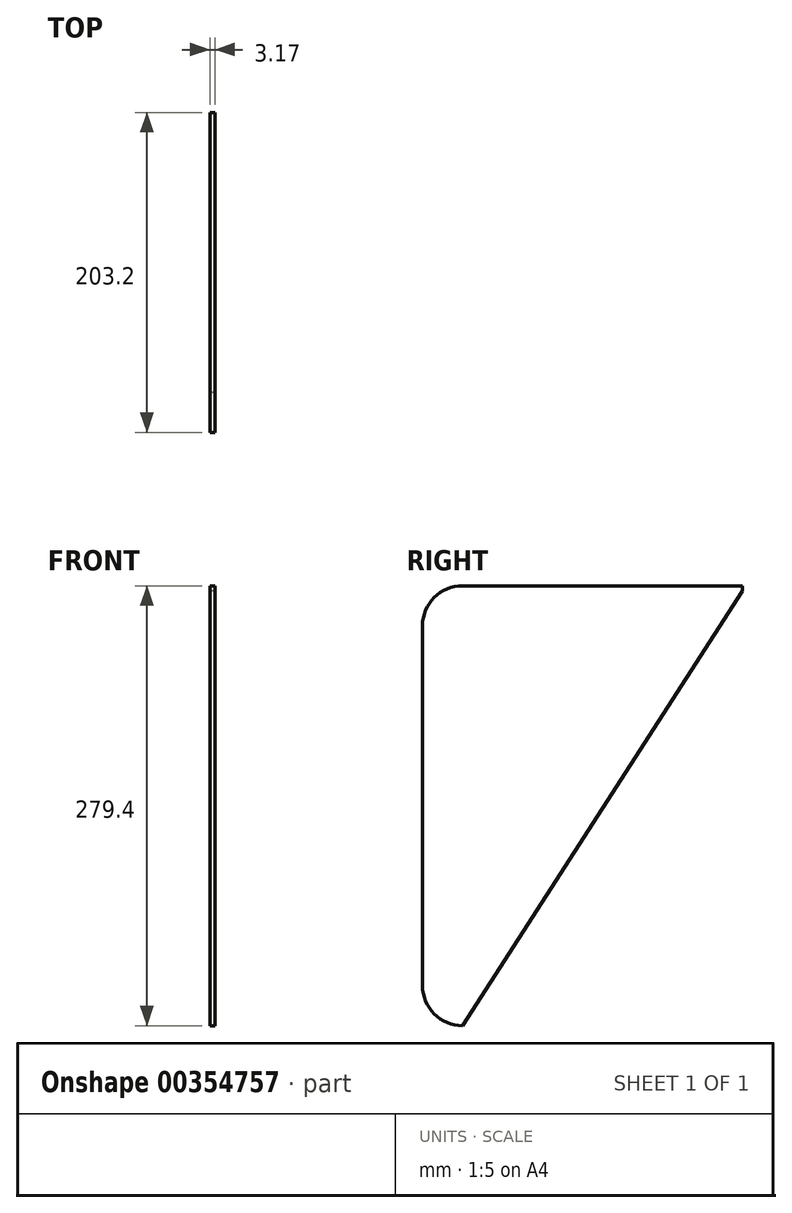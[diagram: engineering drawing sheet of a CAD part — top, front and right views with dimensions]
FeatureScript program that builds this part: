
annotation { "Feature Type Name" : "Feature", "Feature Type Description" : "" }
export const myFeature = defineFeature(function(context is Context, id is Id, definition is map)
    precondition{}
    {
        {
            var Q0;
            Q0=qCreatedBy(makeId("Right.planeOp"),FACE);
            var sketch = newSketch(context, id + "F0", { "sketchPlane" : qUnion([Q0])});
            skLineSegment(sketch, "E0.bottom", {"start": v(88.9, 1.59) * mm, "end": v(-88.9, 1.59) * mm});
            skLineSegment(sketch, "E0.top", {"start": v(88.9, -1.59) * mm, "end": v(-88.9, -1.59) * mm});
            skLineSegment(sketch, "E0.left", {"start": v(88.9, 1.59) * mm, "end": v(88.9, -1.59) * mm});
            skLineSegment(sketch, "E0.right", {"start": v(-88.9, 1.59) * mm, "end": v(-88.9, -1.59) * mm});
            skPoint(sketch, "E0.middle", {"position": v(0, 0) * mm});
            skArc(sketch, "E1", {"start": v(-88.9, 1.59) * mm, "mid": v(-106.86, -5.85) * mm, "end": v(-114.3, -23.81) * mm});
            skArc(sketch, "E2.0", {"start": v(-87.88, -1.61) * mm, "mid": v(-104.25, -7.74) * mm, "end": v(-111.13, -23.81) * mm});
            skLineSegment(sketch, "E3", {"start": v(-114.3, -23.81) * mm, "end": v(-111.13, -23.81) * mm});
            skLineSegment(sketch, "E4", {"start": v(-114.3, -23.81) * mm, "end": v(-114.3, -252.41) * mm});
            skLineSegment(sketch, "E5", {"start": v(-111.13, -23.81) * mm, "end": v(-111.13, -248.5) * mm});
            skLineSegment(sketch, "E6", {"start": v(-114.3, -252.41) * mm, "end": v(-111.13, -248.5) * mm});
            skPoint(sketch, "E7.start.orphan", {"position": v(-111.13, -252.41) * mm});
            skArc(sketch, "E8", {"start": v(-114.3, -252.41) * mm, "mid": v(-106.89, -270.34) * mm, "end": v(-88.98, -277.81) * mm});
            skLineSegment(sketch, "E9", {"start": v(-88.98, -277.81) * mm, "end": v(88.9, -1.59) * mm});
            skSolve(sketch);
        }
        {
            var Q0;
            Q0 = qSketchRegion(id + "F0", true);
            extrude(context, id + "F1", {"entities" : qUnion([Q0]), "depth" : 3.17 * mm});
        }
    });
